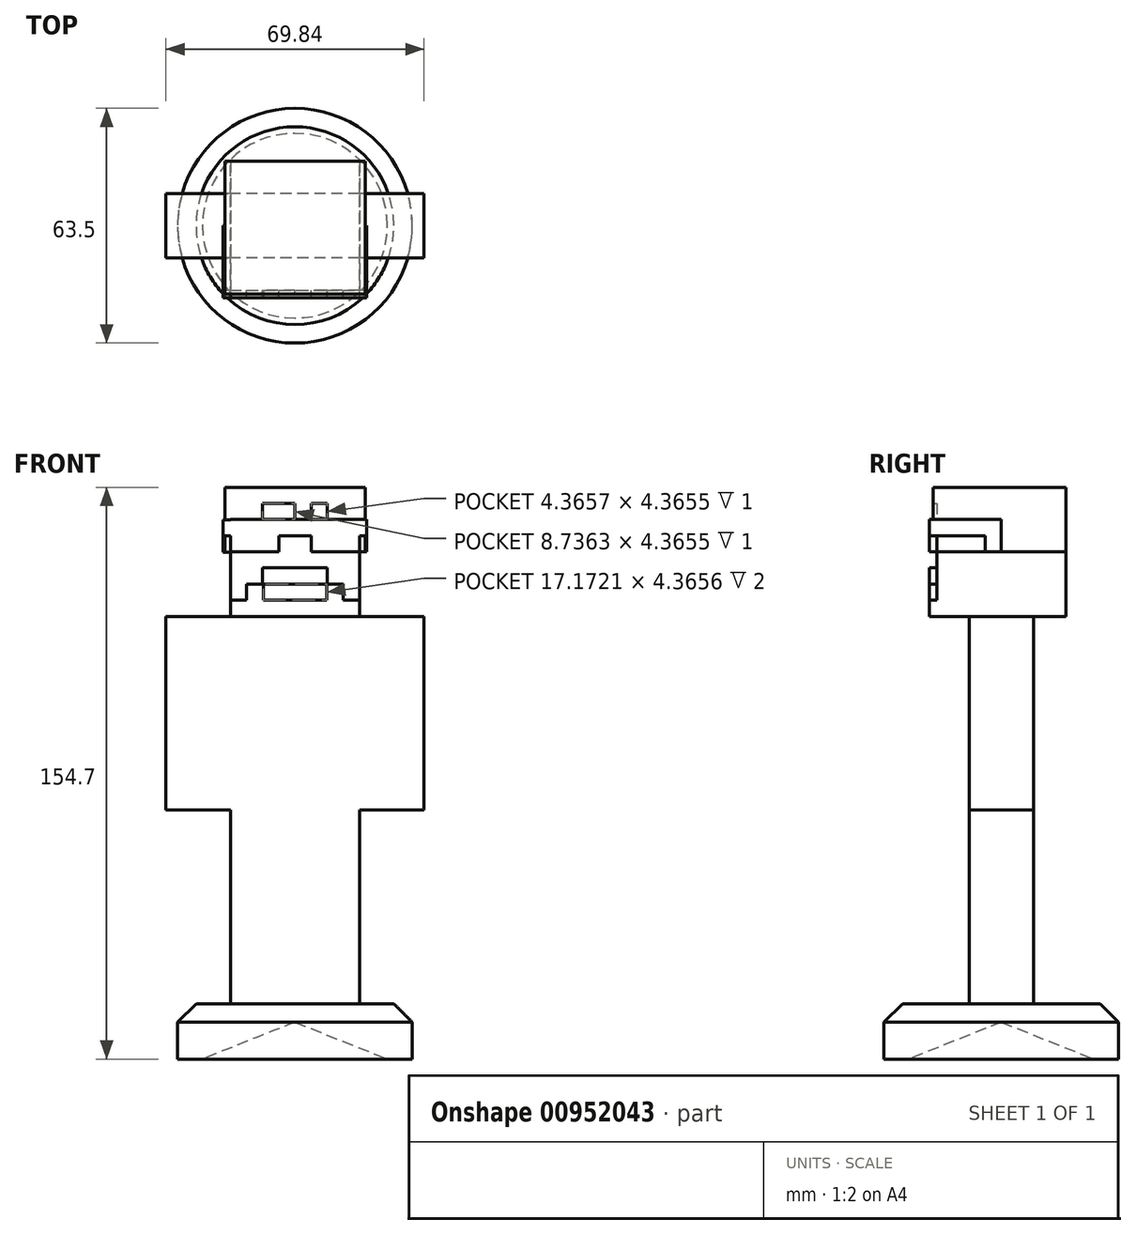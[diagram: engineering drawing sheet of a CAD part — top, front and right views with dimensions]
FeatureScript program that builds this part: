
annotation { "Feature Type Name" : "Feature", "Feature Type Description" : "" }
export const myFeature = defineFeature(function(context is Context, id is Id, definition is map)
    precondition{}
    {
        {
            var Q0;
            Q0=qCreatedBy(makeId("Top.planeOp"),FACE);
            var sketch = newSketch(context, id + "F0", { "sketchPlane" : qUnion([Q0])});
            skCircle(sketch, "E0", {"center": v(0, 0) * mm, "radius": 31.75 * mm});
            skSolve(sketch);
        }
        {
            var Q0;
            Q0=makeQuery(id+"F0.imprint","IMPRINT",FACE,{"disambiguationData":[TD([[makeQuery(id+"F0.imprint","IMPRINT",EDGE,{"derivedFrom":sQuery(id+"F0.wireOp",EDGE,"E0")}),1.0]])]});
            extrude(context, id + "F1", {"entities" : qUnion([Q0]), "depth" : 15 * mm});
        }
        {
            var Q0;
            Q0=makeQuery(id+"F1.opExtrude","CAP_EDGE",EDGE,{"disambiguationData":[OSD([sQuery(id+"F0.wireOp",EDGE,"E0")])],"isStart":false});
            chamfer(context, id + "F2", {"entities" : qUnion([Q0]), "width" : 5 * mm, "tangentPropagation" : true});
        }
        {
            var Q0;
            Q0=makeQuery(id+"F1.opExtrude","CAP_FACE",FACE,{"disambiguationData":[OSD([sQuery(id+"F0.wireOp",EDGE,"E0")])],"isStart":true});
            var sketch = newSketch(context, id + "F3", { "sketchPlane" : qUnion([Q0])});
            skCircle(sketch, "E1", {"center": v(0, 0) * mm, "radius": 25 * mm});
            skSolve(sketch);
        }
        {
            var Q0;
            Q0=makeQuery(id+"F3.imprint","IMPRINT",FACE,{"disambiguationData":[TD([[makeQuery(id+"F3.imprint","IMPRINT",EDGE,{"derivedFrom":sQuery(id+"F3.wireOp",EDGE,"E1")}),1.0]])]});
            extrude(context, id + "F4", {"entities" : qUnion([Q0]), "operationType" : NewBodyOperationType.REMOVE, "oppositeDirection" : true, "depth" : 10 * mm});
        }
        {
            var Q0;
            Q0=makeQuery(id+"F4.boolean.opBoolean","COPY",EDGE,{"derivedFrom":makeQuery(id+"F4.opExtrude","CAP_EDGE",EDGE,{"disambiguationData":[OSD([sQuery(id+"F3.wireOp",EDGE,"E1")])],"isStart":false})});
            chamfer(context, id + "F5", {"entities" : qUnion([Q0]), "chamferType" : ChamferType.TWO_OFFSETS, "width1" : 25 * mm, "oppositeDirection" : false, "width2" : 10 * mm, "tangentPropagation" : true});
        }
        {
            var Q0;
            Q0=makeQuery(id+"F1.opExtrude","CAP_FACE",FACE,{"disambiguationData":[OSD([sQuery(id+"F0.wireOp",EDGE,"E0")])],"isStart":false});
            var sketch = newSketch(context, id + "F6", { "sketchPlane" : qUnion([Q0])});
            skLineSegment(sketch, "E2.bottom", {"start": v(17.46, 8.73) * mm, "end": v(-17.46, 8.73) * mm});
            skLineSegment(sketch, "E2.top", {"start": v(17.46, -8.73) * mm, "end": v(-17.46, -8.73) * mm});
            skLineSegment(sketch, "E2.left", {"start": v(17.46, 8.73) * mm, "end": v(17.46, -8.73) * mm});
            skLineSegment(sketch, "E2.right", {"start": v(-17.46, 8.73) * mm, "end": v(-17.46, -8.73) * mm});
            skPoint(sketch, "E2.middle", {"position": v(0, 0) * mm});
            skSolve(sketch);
        }
        {
            var Q0;
            Q0=makeQuery(id+"F6.imprint","IMPRINT",FACE,{"disambiguationData":[TD([[makeQuery(id+"F6.imprint","IMPRINT",EDGE,{"derivedFrom":sQuery(id+"F6.wireOp",EDGE,"E2.bottom")}),1.0]])]});
            extrude(context, id + "F7", {"entities" : qUnion([Q0]), "operationType" : NewBodyOperationType.ADD, "depth" : 104.78 * mm});
        }
        {
            var Q0;
            Q0=makeQuery(id+"F7.opExtrude","SWEPT_FACE",FACE,{"disambiguationData":[OSD([sQuery(id+"F6.wireOp",EDGE,"E2.left")])]});
            var sketch = newSketch(context, id + "F8", { "sketchPlane" : qUnion([Q0])});
            skLineSegment(sketch, "E3", {"start": v(-8.73, 67.39) * mm, "end": v(8.73, 67.39) * mm});
            skSolve(sketch);
        }
        {
            var Q0;
            Q0=qSketchRegion(id+"F8",true);
            var Q1;
            {var subQ0=sQuery(id+"F8.wireOp",EDGE,"E3");Q1=makeQuery(id+"F8.imprint","IMPRINT",FACE,{"disambiguationData":[TD([[makeQuery(id+"F8.imprint","IMPRINT",EDGE,{"derivedFrom":subQ0}),1.0]])]});}
            extrude(context, id + "F9", {"entities" : qUnion([Q0, Q1]), "operationType" : NewBodyOperationType.ADD, "depth" : 17.46 * mm});
        }
        {
            var Q0;
            Q0=makeQuery(id+"F7.opExtrude","SWEPT_FACE",FACE,{"disambiguationData":[OSD([sQuery(id+"F6.wireOp",EDGE,"E2.right")])]});
            var sketch = newSketch(context, id + "F10", { "sketchPlane" : qUnion([Q0])});
            skLineSegment(sketch, "E4", {"start": v(-8.73, 67.39) * mm, "end": v(8.73, 67.39) * mm});
            skSolve(sketch);
        }
        {
            var Q0;
            {var subQ0=sQuery(id+"F10.wireOp",EDGE,"E4");Q0=makeQuery(id+"F10.imprint","IMPRINT",FACE,{"disambiguationData":[TD([[makeQuery(id+"F10.imprint","IMPRINT",EDGE,{"derivedFrom":subQ0}),1.0]])]});}
            extrude(context, id + "F11", {"entities" : qUnion([Q0]), "operationType" : NewBodyOperationType.ADD, "depth" : 17.46 * mm});
        }
        {
            var Q0;
            {var subQ0=sQuery(id+"F6.wireOp",EDGE,"E2.right");var subQ1=sQuery(id+"F6.wireOp",EDGE,"E2.left");Q0=makeQuery(id+"F11.boolean.opBoolean","MERGE",FACE,{"derivedFrom":[makeQuery(id+"F9.boolean.opBoolean","MERGE",FACE,{"derivedFrom":[makeQuery(id+"F7.opExtrude","CAP_FACE",FACE,{"disambiguationData":[OSD([sQuery(id+"F6.wireOp",EDGE,"E2.bottom"),sQuery(id+"F6.wireOp",EDGE,"E2.top"),subQ1,subQ0])],"isStart":false}),makeQuery(id+"F9.opExtrude","SWEPT_FACE",FACE,{"disambiguationData":[OSD([subQ1])]})]}),makeQuery(id+"F11.opExtrude","SWEPT_FACE",FACE,{"disambiguationData":[OSD([subQ0])]})]});}
            var sketch = newSketch(context, id + "F12", { "sketchPlane" : qUnion([Q0])});
            skLineSegment(sketch, "E5.bottom", {"start": v(17.47, -17.46) * mm, "end": v(-17.47, -17.46) * mm});
            skLineSegment(sketch, "E5.top", {"start": v(17.47, 17.46) * mm, "end": v(-17.47, 17.46) * mm});
            skLineSegment(sketch, "E5.left", {"start": v(17.47, -17.46) * mm, "end": v(17.47, 17.46) * mm});
            skLineSegment(sketch, "E5.right", {"start": v(-17.47, -17.46) * mm, "end": v(-17.47, 17.46) * mm});
            skPoint(sketch, "E5.middle", {"position": v(0, 0) * mm});
            skSolve(sketch);
        }
        {
            var Q0;
            Q0=qSketchRegion(id+"F12",true);
            extrude(context, id + "F13", {"entities" : qUnion([Q0]), "operationType" : NewBodyOperationType.ADD, "depth" : 34.92 * mm});
        }
        {
            var Q0;
            Q0=makeQuery(id+"F13.opExtrude","SWEPT_FACE",FACE,{"disambiguationData":[OSD([sQuery(id+"F12.wireOp",EDGE,"E5.bottom")])]});
            var sketch = newSketch(context, id + "F14", { "sketchPlane" : qUnion([Q0])});
            skLineSegment(sketch, "E6.bottom", {"start": v(17.47, 137.24) * mm, "end": v(4.37, 137.24) * mm});
            skLineSegment(sketch, "E6.top", {"start": v(17.47, 145.97) * mm, "end": v(4.37, 145.97) * mm});
            skLineSegment(sketch, "E6.left", {"start": v(17.47, 137.24) * mm, "end": v(17.47, 145.97) * mm});
            skLineSegment(sketch, "E6.right", {"start": v(4.37, 137.24) * mm, "end": v(4.37, 145.97) * mm});
            skPoint(sketch, "E6.middle", {"position": v(10.92, 141.6) * mm});
            skLineSegment(sketch, "E7.bottom", {"start": v(-17.47, 145.97) * mm, "end": v(-4.37, 145.97) * mm});
            skLineSegment(sketch, "E7.top", {"start": v(-17.47, 137.24) * mm, "end": v(-4.37, 137.24) * mm});
            skLineSegment(sketch, "E7.left", {"start": v(-17.47, 145.97) * mm, "end": v(-17.47, 137.24) * mm});
            skLineSegment(sketch, "E7.right", {"start": v(-4.37, 145.97) * mm, "end": v(-4.37, 137.24) * mm});
            skLineSegment(sketch, "E8.bottom", {"start": v(-4.37, 145.97) * mm, "end": v(4.37, 145.97) * mm});
            skLineSegment(sketch, "E8.top", {"start": v(-4.37, 141.6) * mm, "end": v(4.37, 141.6) * mm});
            skLineSegment(sketch, "E8.left", {"start": v(-4.37, 145.97) * mm, "end": v(-4.37, 141.6) * mm});
            skLineSegment(sketch, "E8.right", {"start": v(4.37, 145.97) * mm, "end": v(4.37, 141.6) * mm});
            skLineSegment(sketch, "E9.bottom", {"start": v(-17.47, 145.97) * mm, "end": v(-8.74, 145.97) * mm});
            skLineSegment(sketch, "E9.top", {"start": v(-17.47, 154.7) * mm, "end": v(-8.74, 154.7) * mm});
            skLineSegment(sketch, "E9.left", {"start": v(-17.47, 145.97) * mm, "end": v(-17.47, 154.7) * mm});
            skLineSegment(sketch, "E9.right", {"start": v(-8.74, 145.97) * mm, "end": v(-8.74, 154.7) * mm});
            skPoint(sketch, "E10.oppositeSnap0", {"position": v(0, 154.7) * mm});
            skPoint(sketch, "E10.oppositeSnap1", {"position": v(-8.74, 150.33) * mm});
            skLineSegment(sketch, "E10.bottom", {"start": v(-8.74, 154.7) * mm, "end": v(0, 154.7) * mm});
            skLineSegment(sketch, "E10.top", {"start": v(-8.74, 150.33) * mm, "end": v(0, 150.33) * mm});
            skLineSegment(sketch, "E10.left", {"start": v(-8.74, 154.7) * mm, "end": v(-8.74, 150.33) * mm});
            skLineSegment(sketch, "E10.right", {"start": v(0, 154.7) * mm, "end": v(0, 150.33) * mm});
            skLineSegment(sketch, "E11.bottom", {"start": v(0, 154.7) * mm, "end": v(4.37, 154.7) * mm});
            skLineSegment(sketch, "E11.top", {"start": v(0, 145.97) * mm, "end": v(4.37, 145.97) * mm});
            skLineSegment(sketch, "E11.left", {"start": v(0, 154.7) * mm, "end": v(0, 145.97) * mm});
            skLineSegment(sketch, "E11.right", {"start": v(4.37, 154.7) * mm, "end": v(4.37, 145.97) * mm});
            skPoint(sketch, "E12.oppositeSnap0", {"position": v(4.37, 150.33) * mm});
            skLineSegment(sketch, "E12.bottom", {"start": v(4.37, 154.7) * mm, "end": v(8.74, 154.7) * mm});
            skLineSegment(sketch, "E12.top", {"start": v(4.37, 150.33) * mm, "end": v(8.74, 150.33) * mm});
            skLineSegment(sketch, "E12.left", {"start": v(4.37, 154.7) * mm, "end": v(4.37, 150.33) * mm});
            skLineSegment(sketch, "E12.right", {"start": v(8.74, 154.7) * mm, "end": v(8.74, 150.33) * mm});
            skLineSegment(sketch, "E13.bottom", {"start": v(8.74, 154.7) * mm, "end": v(17.47, 154.7) * mm});
            skLineSegment(sketch, "E13.top", {"start": v(8.74, 145.97) * mm, "end": v(17.47, 145.97) * mm});
            skLineSegment(sketch, "E13.left", {"start": v(8.74, 154.7) * mm, "end": v(8.74, 145.97) * mm});
            skLineSegment(sketch, "E13.right", {"start": v(17.47, 154.7) * mm, "end": v(17.47, 145.97) * mm});
            skLineSegment(sketch, "E14.bottom", {"start": v(-17.47, 119.78) * mm, "end": v(17.47, 119.78) * mm});
            skLineSegment(sketch, "E14.top", {"start": v(-17.47, 124.14) * mm, "end": v(17.47, 124.14) * mm});
            skLineSegment(sketch, "E14.left", {"start": v(-17.47, 119.78) * mm, "end": v(-17.47, 124.14) * mm});
            skLineSegment(sketch, "E14.right", {"start": v(17.47, 119.78) * mm, "end": v(17.47, 124.14) * mm});
            skPoint(sketch, "E15.firstSnap0", {"position": v(-13.1, 145.97) * mm});
            skPoint(sketch, "E15.oppositeSnap0", {"position": v(13.1, 145.97) * mm});
            skLineSegment(sketch, "E15.bottom", {"start": v(-13.1, 124.14) * mm, "end": v(13.1, 124.14) * mm});
            skLineSegment(sketch, "E15.top", {"start": v(-13.1, 128.5) * mm, "end": v(13.1, 128.5) * mm});
            skLineSegment(sketch, "E15.left", {"start": v(-13.1, 124.14) * mm, "end": v(-13.1, 128.5) * mm});
            skLineSegment(sketch, "E15.right", {"start": v(13.1, 124.14) * mm, "end": v(13.1, 128.5) * mm});
            skLineSegment(sketch, "E16.bottom", {"start": v(-8.74, 128.5) * mm, "end": v(8.74, 128.5) * mm});
            skLineSegment(sketch, "E16.top", {"start": v(-8.74, 132.87) * mm, "end": v(8.74, 132.87) * mm});
            skLineSegment(sketch, "E16.left", {"start": v(-8.74, 128.5) * mm, "end": v(-8.74, 132.87) * mm});
            skLineSegment(sketch, "E16.right", {"start": v(8.74, 128.5) * mm, "end": v(8.74, 132.87) * mm});
            skLineSegment(sketch, "E17.top", {"start": v(-8.74, 124.14) * mm, "end": v(8.74, 124.14) * mm});
            skLineSegment(sketch, "E17.left", {"start": v(-8.74, 128.5) * mm, "end": v(-8.74, 124.14) * mm});
            skLineSegment(sketch, "E17.right", {"start": v(8.74, 128.5) * mm, "end": v(8.74, 124.14) * mm});
            skSolve(sketch);
        }
        {
            var Q0;
            Q0=makeQuery(id+"F13.opExtrude","SWEPT_FACE",FACE,{"disambiguationData":[OSD([sQuery(id+"F12.wireOp",EDGE,"E5.left")])]});
            var sketch = newSketch(context, id + "F15", { "sketchPlane" : qUnion([Q0])});
            skLineSegment(sketch, "E18.bottom", {"start": v(-17.46, 145.97) * mm, "end": v(0, 145.97) * mm});
            skLineSegment(sketch, "E18.top", {"start": v(-17.46, 141.6) * mm, "end": v(0, 141.6) * mm});
            skLineSegment(sketch, "E18.left", {"start": v(-17.46, 145.97) * mm, "end": v(-17.46, 141.6) * mm});
            skLineSegment(sketch, "E18.right", {"start": v(0, 145.97) * mm, "end": v(0, 141.6) * mm});
            skLineSegment(sketch, "E19.bottom", {"start": v(0, 141.6) * mm, "end": v(-4.37, 141.6) * mm});
            skLineSegment(sketch, "E19.top", {"start": v(0, 137.24) * mm, "end": v(-4.37, 137.24) * mm});
            skLineSegment(sketch, "E19.left", {"start": v(0, 141.6) * mm, "end": v(0, 137.24) * mm});
            skLineSegment(sketch, "E19.right", {"start": v(-4.37, 141.6) * mm, "end": v(-4.37, 137.24) * mm});
            skSolve(sketch);
        }
        {
            var Q0;
            Q0=makeQuery(id+"F13.opExtrude","SWEPT_FACE",FACE,{"disambiguationData":[OSD([sQuery(id+"F12.wireOp",EDGE,"E5.right")])]});
            var sketch = newSketch(context, id + "F16", { "sketchPlane" : qUnion([Q0])});
            skLineSegment(sketch, "E20.bottom", {"start": v(17.46, 141.51) * mm, "end": v(0, 141.51) * mm});
            skLineSegment(sketch, "E20.top", {"start": v(17.46, 145.88) * mm, "end": v(0, 145.88) * mm});
            skLineSegment(sketch, "E20.left", {"start": v(17.46, 141.51) * mm, "end": v(17.46, 145.88) * mm});
            skLineSegment(sketch, "E20.right", {"start": v(0, 141.51) * mm, "end": v(0, 145.88) * mm});
            skLineSegment(sketch, "E21.bottom", {"start": v(0, 141.51) * mm, "end": v(4.37, 141.51) * mm});
            skLineSegment(sketch, "E21.top", {"start": v(0, 137.15) * mm, "end": v(4.37, 137.15) * mm});
            skLineSegment(sketch, "E21.left", {"start": v(0, 141.51) * mm, "end": v(0, 137.15) * mm});
            skLineSegment(sketch, "E21.right", {"start": v(4.37, 141.51) * mm, "end": v(4.37, 137.15) * mm});
            skSolve(sketch);
        }
        {
            var Q0;
            Q0=makeQuery(id+"F14.imprint","IMPRINT",FACE,{"disambiguationData":[TD([[makeQuery(id+"F14.imprint","IMPRINT",EDGE,{"derivedFrom":sQuery(id+"F14.wireOp",EDGE,"E12.right")}),1.0]])]});
            var Q1;
            {var subQ0=sQuery(id+"F14.wireOp",EDGE,"E12.bottom");Q1=makeQuery(id+"F14.imprint","IMPRINT",FACE,{"disambiguationData":[TD([[makeQuery(id+"F14.imprint","IMPRINT",EDGE,{"derivedFrom":subQ0}),1.0]])]});}
            var Q2;
            Q2=makeQuery(id+"F14.imprint","IMPRINT",FACE,{"disambiguationData":[TD([[makeQuery(id+"F14.imprint","IMPRINT",EDGE,{"derivedFrom":sQuery(id+"F14.wireOp",EDGE,"E10.right")}),1.0]])]});
            var Q3;
            {var subQ0=sQuery(id+"F14.wireOp",EDGE,"E10.bottom");Q3=makeQuery(id+"F14.imprint","IMPRINT",FACE,{"disambiguationData":[TD([[makeQuery(id+"F14.imprint","IMPRINT",EDGE,{"derivedFrom":subQ0}),1.0]])]});}
            var Q4;
            {var subQ5=sQuery(id+"F14.wireOp",EDGE,"E9.top");Q4=makeQuery(id+"F14.imprint","IMPRINT",FACE,{"disambiguationData":[TD([[makeQuery(id+"F14.imprint","IMPRINT",EDGE,{"derivedFrom":subQ5}),1.0]])]});}
            extrude(context, id + "F17", {"entities" : qUnion([Q0, Q1, Q2, Q3, Q4]), "operationType" : NewBodyOperationType.ADD, "depth" : 1 * mm});
        }
        {
            var Q0;
            {var subQ5=sQuery(id+"F14.wireOp",EDGE,"E6.bottom");Q0=makeQuery(id+"F14.imprint","IMPRINT",FACE,{"disambiguationData":[TD([[makeQuery(id+"F14.imprint","IMPRINT",EDGE,{"derivedFrom":subQ5}),-1.0]])]});}
            var Q1;
            {var subQ6=sQuery(id+"F14.wireOp",EDGE,"E8.top");Q1=makeQuery(id+"F14.imprint","IMPRINT",FACE,{"disambiguationData":[TD([[makeQuery(id+"F14.imprint","IMPRINT",EDGE,{"derivedFrom":subQ6}),1.0]])]});}
            var Q2;
            {var subQ1=sQuery(id+"F14.wireOp",EDGE,"E7.top");Q2=makeQuery(id+"F14.imprint","IMPRINT",FACE,{"disambiguationData":[TD([[makeQuery(id+"F14.imprint","IMPRINT",EDGE,{"derivedFrom":subQ1}),1.0]])]});}
            var Q3;
            Q3=makeQuery(id+"F14.imprint","IMPRINT",FACE,{"disambiguationData":[TD([[makeQuery(id+"F14.imprint","IMPRINT",EDGE,{"derivedFrom":sQuery(id+"F14.wireOp",EDGE,"E16.top")}),-1.0]])]});
            var Q4;
            {var subQ2=sQuery(id+"F14.wireOp",EDGE,"E15.left");Q4=makeQuery(id+"F14.imprint","IMPRINT",FACE,{"disambiguationData":[TD([[makeQuery(id+"F14.imprint","IMPRINT",EDGE,{"derivedFrom":subQ2}),-1.0]])]});}
            var Q5;
            Q5=makeQuery(id+"F14.imprint","IMPRINT",FACE,{"disambiguationData":[TD([[makeQuery(id+"F14.imprint","IMPRINT",EDGE,{"derivedFrom":sQuery(id+"F14.wireOp",EDGE,"E14.bottom")}),-1.0]])]});
            var Q6;
            {var subQ0=sQuery(id+"F14.wireOp",EDGE,"E15.right");Q6=makeQuery(id+"F14.imprint","IMPRINT",FACE,{"disambiguationData":[TD([[makeQuery(id+"F14.imprint","IMPRINT",EDGE,{"derivedFrom":subQ0}),1.0]])]});}
            var Q7;
            {var subQ0=sQuery(id+"F14.wireOp",EDGE,"E17.left");Q7=makeQuery(id+"F14.imprint","IMPRINT",FACE,{"disambiguationData":[TD([[makeQuery(id+"F14.imprint","IMPRINT",EDGE,{"derivedFrom":subQ0}),1.0]])]});}
            extrude(context, id + "F18", {"entities" : qUnion([Q0, Q1, Q2, Q3, Q4, Q5, Q6, Q7]), "operationType" : NewBodyOperationType.ADD, "depth" : 2 * mm});
        }
        {
            var Q0;
            Q0=makeQuery(id+"F15.imprint","IMPRINT",FACE,{"disambiguationData":[TD([[makeQuery(id+"F15.imprint","IMPRINT",EDGE,{"derivedFrom":sQuery(id+"F15.wireOp",EDGE,"E18.bottom")}),-1.0]])]});
            var Q1;
            Q1=makeQuery(id+"F15.imprint","IMPRINT",FACE,{"disambiguationData":[TD([[makeQuery(id+"F15.imprint","IMPRINT",EDGE,{"derivedFrom":sQuery(id+"F15.wireOp",EDGE,"E19.top")}),-1.0]])]});
            var Q2;
            Q2=makeQuery(id+"F16.imprint","IMPRINT",FACE,{"disambiguationData":[TD([[makeQuery(id+"F16.imprint","IMPRINT",EDGE,{"derivedFrom":sQuery(id+"F16.wireOp",EDGE,"E21.top")}),1.0]])]});
            extrude(context, id + "F19", {"entities" : qUnion([Q0, Q1, Q2]), "operationType" : NewBodyOperationType.ADD, "depth" : 2 * mm});
        }
        {
            var Q0;
            Q0=makeQuery(id+"F16.imprint","IMPRINT",FACE,{"disambiguationData":[TD([[makeQuery(id+"F16.imprint","IMPRINT",EDGE,{"derivedFrom":sQuery(id+"F16.wireOp",EDGE,"E21.top")}),1.0]])]});
            var Q1;
            Q1=makeQuery(id+"F16.imprint","IMPRINT",FACE,{"disambiguationData":[TD([[makeQuery(id+"F16.imprint","IMPRINT",EDGE,{"derivedFrom":sQuery(id+"F16.wireOp",EDGE,"E20.top")}),1.0]])]});
            extrude(context, id + "F20", {"entities" : qUnion([Q0, Q1]), "operationType" : NewBodyOperationType.ADD, "depth" : 2 * mm});
        }
        {
            var Q0;
            Q0=makeQuery(id+"F19.opExtrude","SWEPT_FACE",FACE,{"disambiguationData":[OSD([sQuery(id+"F15.wireOp",EDGE,"E18.left")])]});
            var Q1;
            Q1=makeQuery(id+"F20.opExtrude","SWEPT_FACE",FACE,{"disambiguationData":[OSD([sQuery(id+"F16.wireOp",EDGE,"E20.left")])]});
            extrude(context, id + "F21", {"entities" : qUnion([Q0, Q1]), "operationType" : NewBodyOperationType.ADD, "depth" : 2 * mm});
        }
        {
            var Q0;
            Q0=makeQuery(id+"F18.opExtrude","CAP_FACE",FACE,{"disambiguationData":[OSD([sQuery(id+"F14.wireOp",EDGE,"E14.bottom"),sQuery(id+"F14.wireOp",EDGE,"E14.top"),sQuery(id+"F14.wireOp",EDGE,"E14.left"),sQuery(id+"F14.wireOp",EDGE,"E14.right"),sQuery(id+"F14.wireOp",EDGE,"E15.top"),sQuery(id+"F14.wireOp",EDGE,"E15.left"),sQuery(id+"F14.wireOp",EDGE,"E15.right"),sQuery(id+"F14.wireOp",EDGE,"E16.top"),sQuery(id+"F14.wireOp",EDGE,"E16.left"),sQuery(id+"F14.wireOp",EDGE,"E16.right")])],"isStart":false});
            var sketch = newSketch(context, id + "F22", { "sketchPlane" : qUnion([Q0])});
            skLineSegment(sketch, "E22.bottom", {"start": v(-8.59, 128.5) * mm, "end": v(8.59, 128.5) * mm});
            skLineSegment(sketch, "E22.top", {"start": v(-8.59, 124.14) * mm, "end": v(8.59, 124.14) * mm});
            skLineSegment(sketch, "E22.left", {"start": v(-8.59, 128.5) * mm, "end": v(-8.59, 124.14) * mm});
            skLineSegment(sketch, "E22.right", {"start": v(8.59, 128.5) * mm, "end": v(8.59, 124.14) * mm});
            skSolve(sketch);
        }
        {
            var Q0;
            Q0=qSketchRegion(id+"F22",true);
            extrude(context, id + "F23", {"entities" : qUnion([Q0]), "operationType" : NewBodyOperationType.REMOVE, "oppositeDirection" : true, "depth" : 2 * mm, "offsetDistance" : 25 * mm});
        }
        {
            var Q0;
            {var subQ20=sQuery(id+"F16.wireOp",EDGE,"E20.top");Q0=makeQuery(id+"F16.imprint","IMPRINT",FACE,{"disambiguationData":[TD([[makeQuery(id+"F16.imprint","IMPRINT",EDGE,{"derivedFrom":subQ20}),-1.0]])]});}
            var sketch = newSketch(context, id + "F24", { "sketchPlane" : qUnion([Q0])});
            skLineSegment(sketch, "E23.bottom", {"start": v(-17.46, 154.7) * mm, "end": v(17.46, 154.7) * mm});
            skLineSegment(sketch, "E23.top", {"start": v(-17.46, 137.15) * mm, "end": v(17.46, 137.15) * mm});
            skLineSegment(sketch, "E23.left", {"start": v(-17.46, 154.7) * mm, "end": v(-17.46, 137.15) * mm});
            skLineSegment(sketch, "E23.right", {"start": v(17.46, 154.7) * mm, "end": v(17.46, 137.15) * mm});
            skSolve(sketch);
        }
        {
            var Q0;
            Q0=qSketchRegion(id+"F24",true);
            extrude(context, id + "F25", {"entities" : qUnion([Q0]), "operationType" : NewBodyOperationType.ADD, "depth" : 1.5 * mm, "offsetDistance" : 25 * mm});
        }
        {
            var Q0;
            {var subQ16=sQuery(id+"F15.wireOp",EDGE,"E18.bottom");Q0=makeQuery(id+"F15.imprint","IMPRINT",FACE,{"disambiguationData":[TD([[makeQuery(id+"F15.imprint","IMPRINT",EDGE,{"derivedFrom":subQ16}),1.0]])]});}
            var sketch = newSketch(context, id + "F26", { "sketchPlane" : qUnion([Q0])});
            skLineSegment(sketch, "E24.bottom", {"start": v(-17.46, 154.7) * mm, "end": v(17.46, 154.7) * mm});
            skLineSegment(sketch, "E24.top", {"start": v(-17.46, 137.24) * mm, "end": v(17.46, 137.24) * mm});
            skLineSegment(sketch, "E24.left", {"start": v(-17.46, 154.7) * mm, "end": v(-17.46, 137.24) * mm});
            skLineSegment(sketch, "E24.right", {"start": v(17.46, 154.7) * mm, "end": v(17.46, 137.24) * mm});
            skSolve(sketch);
        }
        {
            var Q0;
            Q0=qSketchRegion(id+"F26",true);
            extrude(context, id + "F27", {"entities" : qUnion([Q0]), "operationType" : NewBodyOperationType.ADD, "depth" : 1.5 * mm, "offsetDistance" : 25 * mm});
        }
        {
            var Q0;
            {var subQ0=sQuery(id+"F15.wireOp",EDGE,"E18.bottom");var subQ4=sQuery(id+"F26.wireOp",EDGE,"E24.left");Q0=makeQuery(id+"F27.boolean.opBoolean","SPLIT",FACE,{"disambiguationData":[TD([makeQuery(id+"F19.opExtrude","SWEPT_FACE",FACE,{"disambiguationData":[OSD([subQ0])]})])],"derivedFrom":makeQuery(id+"F27.opExtrude","SWEPT_FACE",FACE,{"disambiguationData":[OSD([subQ4])]})});}
            extrude(context, id + "F28", {"entities" : qUnion([Q0]), "operationType" : NewBodyOperationType.ADD, "depth" : 1 * mm, "offsetDistance" : 25 * mm});
        }
        {
            var Q0;
            Q0=makeQuery(id+"F25.boolean.opBoolean","SPLIT",FACE,{"derivedFrom":makeQuery(id+"F25.opExtrude","SWEPT_FACE",FACE,{"disambiguationData":[OSD([sQuery(id+"F24.wireOp",EDGE,"E23.right")])]})});
            extrude(context, id + "F29", {"entities" : qUnion([Q0]), "operationType" : NewBodyOperationType.ADD, "depth" : 1 * mm, "offsetDistance" : 25 * mm});
        }
    });
